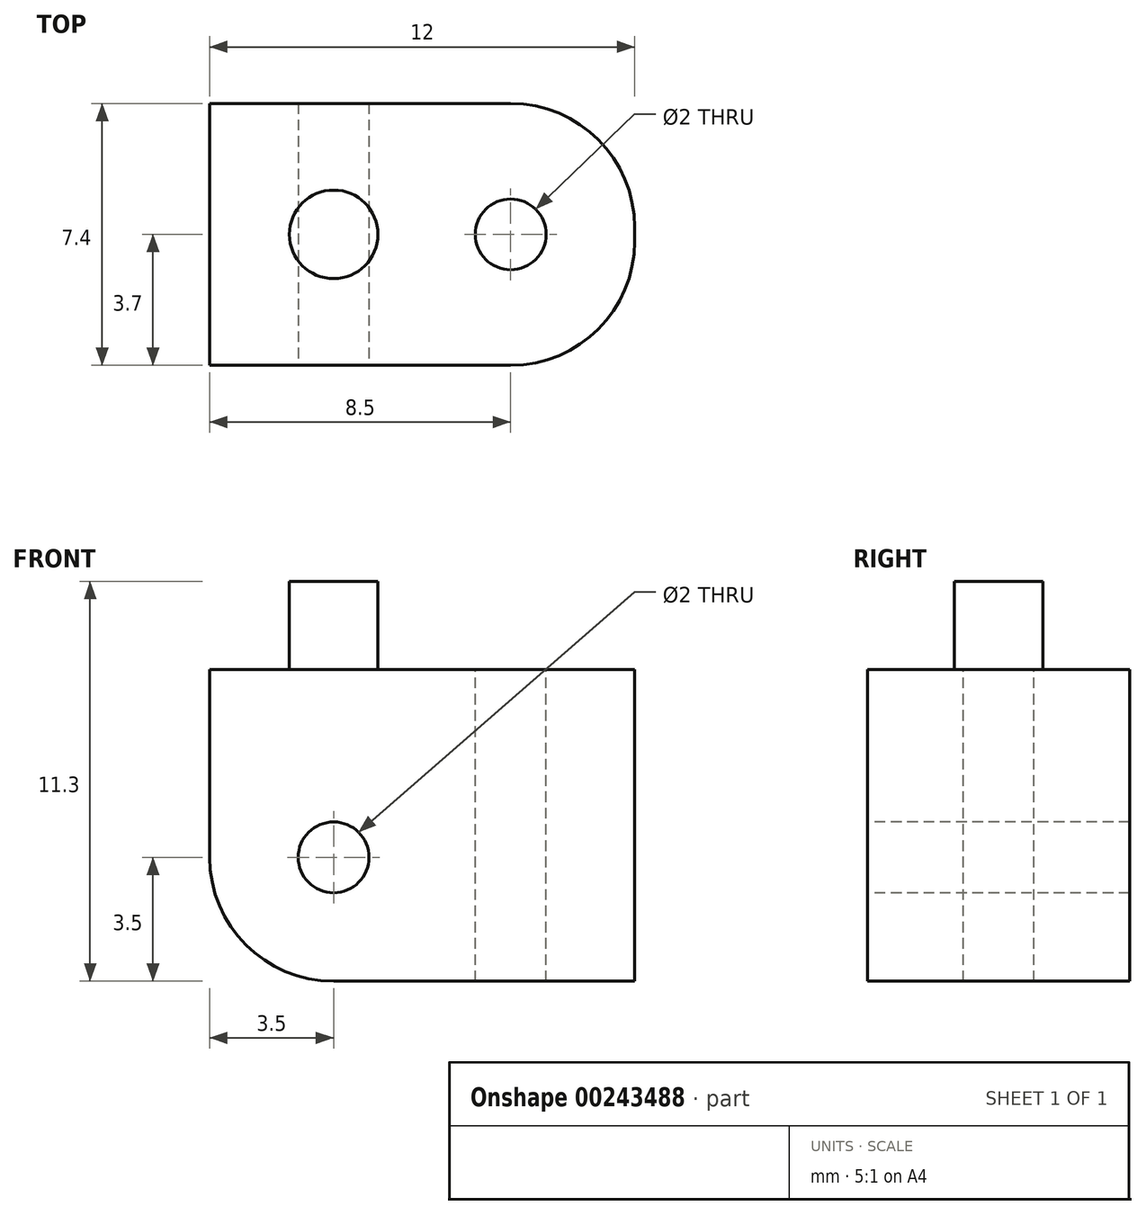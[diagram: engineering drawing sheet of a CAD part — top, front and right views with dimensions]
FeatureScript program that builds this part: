
annotation { "Feature Type Name" : "Feature", "Feature Type Description" : "" }
export const myFeature = defineFeature(function(context is Context, id is Id, definition is map)
    precondition{}
    {
        {
            var Q0;
            Q0=qCreatedBy(makeId("Top.planeOp"),FACE);
            var sketch = newSketch(context, id + "F0", { "sketchPlane" : qUnion([Q0])});
            skLineSegment(sketch, "E0.bottom", {"start": v(0, 0) * mm, "end": v(12, 0) * mm});
            skLineSegment(sketch, "E0.top", {"start": v(0, 7.4) * mm, "end": v(12, 7.4) * mm});
            skLineSegment(sketch, "E0.left", {"start": v(0, 0) * mm, "end": v(0, 7.4) * mm});
            skLineSegment(sketch, "E0.right", {"start": v(12, 0) * mm, "end": v(12, 7.4) * mm});
            skSolve(sketch);
        }
        {
            var Q0;
            Q0 = qSketchRegion(id + "F0", true);
            extrude(context, id + "F1", {"entities" : qUnion([Q0]), "depth" : 8.8 * mm, "offsetDistance" : 25 * mm});
        }
        {
            var Q0;
            Q0=makeQuery(id+"F1.opExtrude","SWEPT_FACE",FACE,{"disambiguationData":[OSD([sQuery(id+"F0.wireOp",EDGE,"E0.bottom")])]});
            var sketch = newSketch(context, id + "F2", { "sketchPlane" : qUnion([Q0])});
            skCircle(sketch, "E1", {"center": v(3.5, 3.5) * mm, "radius": 1 * mm});
            skSolve(sketch);
        }
        {
            var Q0;
            Q0=makeQuery(id+"F2.imprint","IMPRINT",FACE,{"disambiguationData":[TD([[makeQuery(id+"F2.imprint","IMPRINT",EDGE,{"derivedFrom":sQuery(id+"F2.wireOp",EDGE,"E1")}),1.0]])]});
            extrude(context, id + "F3", {"entities" : qUnion([Q0]), "operationType" : NewBodyOperationType.REMOVE, "oppositeDirection" : true, "depth" : 25 * mm, "offsetDistance" : 25 * mm});
        }
        {
            var Q0;
            Q0=makeQuery(id+"F1.opExtrude","CAP_EDGE",EDGE,{"disambiguationData":[OSD([sQuery(id+"F0.wireOp",EDGE,"E0.left")])],"isStart":true});
            fillet(context, id + "F4", {"entities" : qUnion([Q0]), "tangentPropagation" : true, "radius" : 3.5 * mm, "defaultsChanged" : true, "vertexSettings" : [], "allowEdgeOverflow" : false});
        }
        {
            var Q0;
            Q0=makeQuery(id+"F1.opExtrude","SWEPT_EDGE",EDGE,{"disambiguationData":[OSD([sQuery(id+"F0.wireOp",EDGE,"E0.bottom"),sQuery(id+"F0.wireOp",EDGE,"E0.right")])]});
            var Q1;
            Q1=makeQuery(id+"F1.opExtrude","SWEPT_EDGE",EDGE,{"disambiguationData":[OSD([sQuery(id+"F0.wireOp",EDGE,"E0.top"),sQuery(id+"F0.wireOp",EDGE,"E0.right")])]});
            fillet(context, id + "F5", {"entities" : qUnion([Q0, Q1]), "tangentPropagation" : true, "radius" : 3.5 * mm, "defaultsChanged" : true, "vertexSettings" : [], "allowEdgeOverflow" : false});
        }
        {
            var Q0;
            Q0=makeQuery(id+"F1.opExtrude","CAP_FACE",FACE,{"disambiguationData":[OSD([sQuery(id+"F0.wireOp",EDGE,"E0.bottom"),sQuery(id+"F0.wireOp",EDGE,"E0.top"),sQuery(id+"F0.wireOp",EDGE,"E0.left"),sQuery(id+"F0.wireOp",EDGE,"E0.right")])],"isStart":false});
            var sketch = newSketch(context, id + "F6", { "sketchPlane" : qUnion([Q0])});
            skLineSegment(sketch, "E2", {"start": v(0, 3.7) * mm, "end": v(12, 3.7) * mm, "construction": true});
            skCircle(sketch, "E3", {"center": v(8.5, 3.7) * mm, "radius": 1 * mm});
            skCircle(sketch, "E4", {"center": v(3.5, 3.7) * mm, "radius": 1.25 * mm});
            skSolve(sketch);
        }
        {
            var Q0;
            Q0=makeQuery(id+"F6.imprint","IMPRINT",FACE,{"disambiguationData":[TD([[makeQuery(id+"F6.imprint","IMPRINT",EDGE,{"derivedFrom":sQuery(id+"F6.wireOp",EDGE,"E4")}),1.0]])]});
            extrude(context, id + "F7", {"entities" : qUnion([Q0]), "operationType" : NewBodyOperationType.ADD, "depth" : 2.5 * mm, "offsetDistance" : 25 * mm});
        }
        {
            var Q0;
            Q0=makeQuery(id+"F6.imprint","IMPRINT",FACE,{"disambiguationData":[TD([[makeQuery(id+"F6.imprint","IMPRINT",EDGE,{"derivedFrom":sQuery(id+"F6.wireOp",EDGE,"E3")}),1.0]])]});
            extrude(context, id + "F8", {"entities" : qUnion([Q0]), "operationType" : NewBodyOperationType.REMOVE, "oppositeDirection" : true, "depth" : 25 * mm, "offsetDistance" : 25 * mm});
        }
    });
